# Revit family: SW100 Arm system PUSH_GOTOVO
name_source: partatom
category: Doors
revit_build: Autodesk Revit Architecture 2014 (Build: 20130308_1515(x64)
units: mm (PartAtom-declared; Revit-internal decimal feet)

## types (1)
- SW100 Arm system PUSH_GOTOVO
    Analytic Construction = <None>
    BIMobject category = Swing Doors
    Date of publishing = 2015-02-23
    Depth = 0.00
    Depth (mm) = 0' - 0"
    Edition number = 1
    Function = Interior
    Height (mm) = 0' - 0"
    IFC Classification = Door
    Manufacturer name = Besam-North America
    Material main = Aluminium
    Material secondary = Aluminium
    Nominal height = 0.00
    Nominal width = 0.00
    Product Guid = 3603ede4-d252-4fa3-ada0-ee24d92eecad
    Product SKU = SW100_SM
    Product data url = http://besam-na.bimobject.com
    Product family = Swing
    Product group = Surface Mount
    QR code = http://besam-na.bimobject.com
    UNSPSC Code = 30171511
    Uniclass 1.4 Code = L81323
    Uniclass 1.4 Description = Swings
    Wall Closure = By host
    Weight Net (Kg) = 0
    Width (mm) = 0' - 0"

## geometry (parser evidence)
native form markers: Sweep x2
no freeform markers — native parametric forms only
